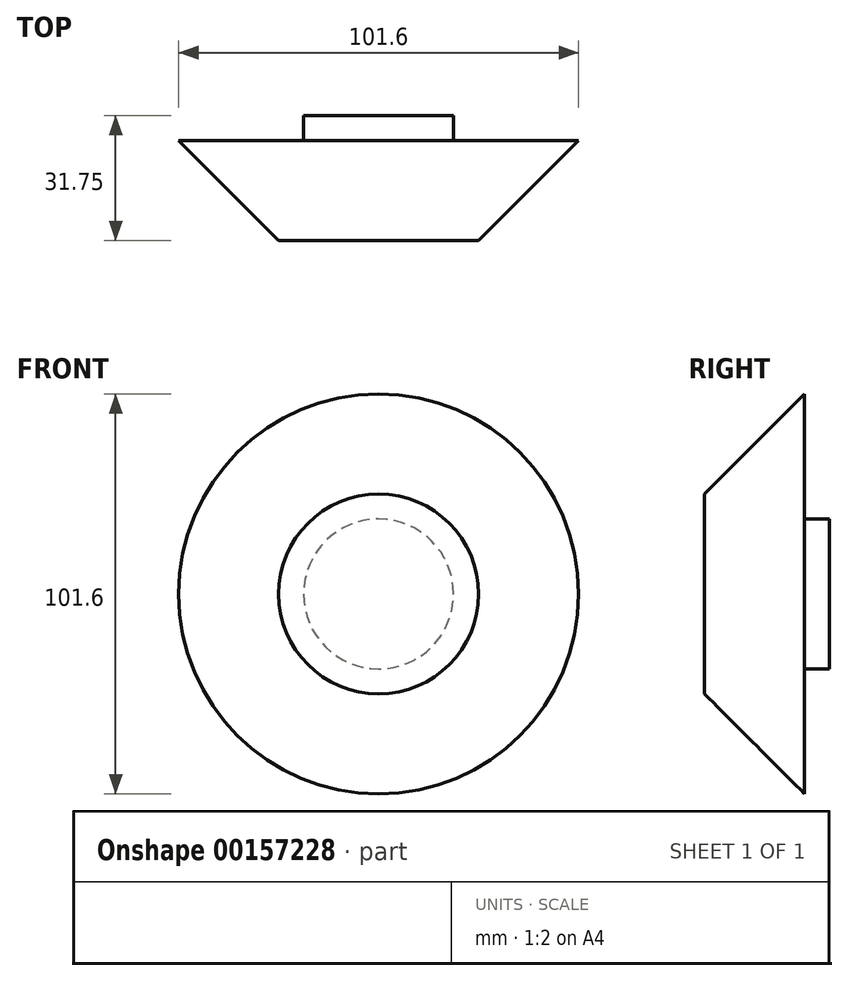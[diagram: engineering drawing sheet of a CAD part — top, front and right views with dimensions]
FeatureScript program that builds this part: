
annotation { "Feature Type Name" : "Feature", "Feature Type Description" : "" }
export const myFeature = defineFeature(function(context is Context, id is Id, definition is map)
    precondition{}
    {
        {
            var Q0;
            Q0=qCreatedBy(makeId("Front.planeOp"),FACE);
            var sketch = newSketch(context, id + "F0", { "sketchPlane" : qUnion([Q0])});
            skCircle(sketch, "E0", {"center": v(0, 0) * mm, "radius": 50.8 * mm});
            skSolve(sketch);
        }
        {
            var Q0;
            Q0=qCreatedBy(makeId("Front.planeOp"),FACE);
            cPlane(context, id + "F1", {"entities" : qUnion([Q0]), "cplaneType" : CPlaneType.OFFSET, "offset" : 25.4 * mm, "width" : 152.4 * mm, "height" : 152.4 * mm});
        }
        {
            var Q0;
            Q0=qCreatedBy(id+"F1.planeOp",FACE);
            var sketch = newSketch(context, id + "F2", { "sketchPlane" : qUnion([Q0])});
            skCircle(sketch, "E1", {"center": v(0, 0) * mm, "radius": 25.4 * mm});
            skSolve(sketch);
        }
        {
            var Q0;
            Q0=makeQuery(id+"F0.imprint","IMPRINT",FACE,{"disambiguationData":[TD([[makeQuery(id+"F0.imprint","IMPRINT",EDGE,{"derivedFrom":sQuery(id+"F0.wireOp",EDGE,"E0")}),1.0]])]});
            var Q1;
            Q1=makeQuery(id+"F2.imprint","IMPRINT",FACE,{"disambiguationData":[TD([[makeQuery(id+"F2.imprint","IMPRINT",EDGE,{"derivedFrom":sQuery(id+"F2.wireOp",EDGE,"E1")}),1.0]])]});
            loft(context, id + "F3", {"sheetProfilesArray" : [{ "sheetProfileEntities" : qUnion([Q0]) }, { "sheetProfileEntities" : qUnion([Q1]) }]});
        }
        {
            var Q0;
            Q0=makeQuery(id+"F3.opLoft","CAP_FACE",FACE,{"disambiguationData":[OSD([makeQuery(id+"F0.imprint","IMPRINT",FACE,{"disambiguationData":[TD([[makeQuery(id+"F0.imprint","IMPRINT",EDGE,{"derivedFrom":sQuery(id+"F0.wireOp",EDGE,"E0")}),1.0]])]})])],"isStart":true});
            var sketch = newSketch(context, id + "F4", { "sketchPlane" : qUnion([Q0])});
            skCircle(sketch, "E2.0.0", {"center": v(0, 0) * mm, "radius": 50.8 * mm});
            skCircle(sketch, "E3", {"center": v(0, 0) * mm, "radius": 19.05 * mm});
            skSolve(sketch);
        }
        {
            var Q0;
            Q0=makeQuery(id+"F4.imprint","IMPRINT",FACE,{"disambiguationData":[TD([[makeQuery(id+"F4.imprint","IMPRINT",EDGE,{"derivedFrom":sQuery(id+"F4.wireOp",EDGE,"E3")}),1.0]])]});
            extrude(context, id + "F5", {"entities" : qUnion([Q0]), "operationType" : NewBodyOperationType.ADD, "depth" : 6.35 * mm});
        }
    });
